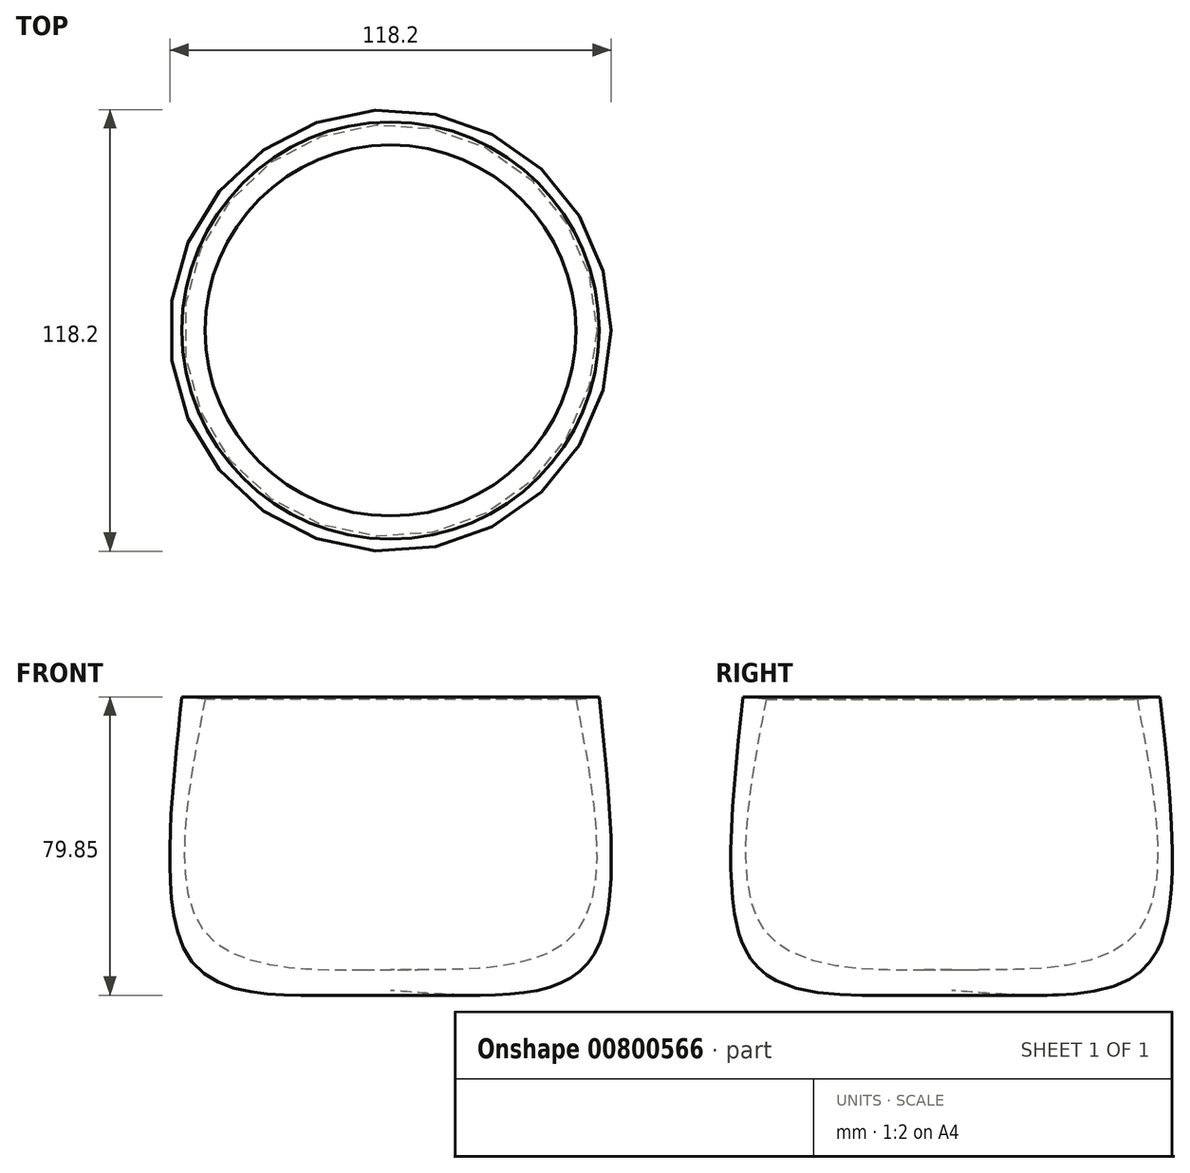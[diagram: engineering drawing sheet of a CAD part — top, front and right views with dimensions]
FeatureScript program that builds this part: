
annotation { "Feature Type Name" : "Feature", "Feature Type Description" : "" }
export const myFeature = defineFeature(function(context is Context, id is Id, definition is map)
    precondition{}
    {
        {
            var Q0;
            Q0=qCreatedBy(makeId("Front.planeOp"),FACE);
            var sketch = newSketch(context, id + "F0", { "sketchPlane" : qUnion([Q0])});
            skLineSegment(sketch, "E0", {"start": v(0, 34.35) * mm, "end": v(0, -41.15) * mm});
            skFitSpline(sketch, "E1", {"points": [v(55.85, 42.4) * mm, v(55.85, -23.83) * mm, v(39.14, -36.2) * mm, v(0, -36.2) * mm], "startDerivative": vector(19.68, -184.86) * mm, "endDerivative": vector(-129.6, 9.92) * mm});
            skFitSpline(sketch, "E2", {"points": [v(49.66, 41.77) * mm, v(49.04, -21.35) * mm, v(14.39, -30.63) * mm, v(0, -30.63) * mm], "startDerivative": vector(32.8, -172.88) * mm, "endDerivative": vector(-55.4, 0.65) * mm});
            skFitSpline(sketch, "E3", {"points": [v(49.66, 41.77) * mm, v(55.85, 42.4) * mm], "startDerivative": vector(6.19, 0.62) * mm, "endDerivative": vector(6.19, 0.62) * mm});
            skSolve(sketch);
        }
        {
            var Q0;
            {var subQ0=sQuery(id+"F0.wireOp",EDGE,"E1");Q0=makeQuery(id+"F0.imprint","IMPRINT",FACE,{"disambiguationData":[TD([[makeQuery(id+"F0.imprint","IMPRINT",EDGE,{"derivedFrom":subQ0}),-1.0]])]});}
            var Q1;
            Q1=sQuery(id+"F0.wireOp",EDGE,"E0");
            revolve(context, id + "F1", {"surfaceOperationType" : NewSurfaceOperationType.NEW, "entities" : qUnion([Q0]), "axis" : qUnion([Q1]), "revolveType" : RevolveType.FULL});
        }
        {
            var Q0;
            Q0=qCreatedBy(makeId("Front.planeOp"),FACE);
            var sketch = newSketch(context, id + "F2", { "sketchPlane" : qUnion([Q0])});
            skLineSegment(sketch, "E4", {"start": v(35.43, 29.4) * mm, "end": v(60.7, 29.4) * mm});
            skLineSegment(sketch, "E5", {"start": v(75.7, 14.4) * mm, "end": v(75.7, -14.4) * mm});
            skLineSegment(sketch, "E6", {"start": v(60.7, -29.4) * mm, "end": v(36.05, -29.4) * mm});
            skPoint(sketch, "E7.visualSharp", {"position": v(75.7, 29.4) * mm});
            skArc(sketch, "E7.filletArc", {"start": v(75.7, 14.4) * mm, "mid": v(71.31, 25) * mm, "end": v(60.7, 29.4) * mm});
            skPoint(sketch, "E8.visualSharp", {"position": v(75.7, -29.4) * mm});
            skArc(sketch, "E8.filletArc", {"start": v(60.7, -29.4) * mm, "mid": v(71.31, -25) * mm, "end": v(75.7, -14.4) * mm});
            skLineSegment(sketch, "E9", {"start": v(0, 29.4) * mm, "end": v(0, -30.46) * mm});
            skLineSegment(sketch, "E10", {"start": v(35.43, 29.4) * mm, "end": v(14.03, 29.4) * mm});
            skLineSegment(sketch, "E11", {"start": v(14.03, 29.4) * mm, "end": v(14.03, -30) * mm});
            skLineSegment(sketch, "E12", {"start": v(14.03, -30) * mm, "end": v(36.05, -29.4) * mm});
            skSolve(sketch);
        }
        {
            var Q0;
            Q0=qCreatedBy(makeId("Right.planeOp"),FACE);
            var sketch = newSketch(context, id + "F3", { "sketchPlane" : qUnion([Q0])});
            skCircle(sketch, "E13", {"center": v(197.25, 38.45) * mm, "radius": 3.87 * mm});
            skCircle(sketch, "E14", {"center": v(0, -30.43) * mm, "radius": 6.75 * mm});
            skCircle(sketch, "E15", {"center": v(0, 28.97) * mm, "radius": 5.76 * mm});
            skSolve(sketch);
        }
        {
            var Q0;
            Q0=makeQuery(id+"F3.imprint","IMPRINT",FACE,{"disambiguationData":[TD([[makeQuery(id+"F3.imprint","IMPRINT",EDGE,{"derivedFrom":sQuery(id+"F3.wireOp",EDGE,"E15")}),1.0]])]});
            var Q1;
            Q1=sQuery(id+"F3.wireOp",EDGE,"E15");
            var Q2;
            Q2=sQuery(id+"F2.wireOp",EDGE,"E10");
            var Q3;
            Q3=sQuery(id+"F2.wireOp",EDGE,"E4");
            var Q4;
            Q4=sQuery(id+"F2.wireOp",EDGE,"E7.filletArc");
            var Q5;
            Q5=sQuery(id+"F2.wireOp",EDGE,"E5");
            var Q6;
            Q6=sQuery(id+"F2.wireOp",EDGE,"E8.filletArc");
            var Q7;
            Q7=sQuery(id+"F2.wireOp",EDGE,"E6");
            var Q8;
            Q8=sQuery(id+"F2.wireOp",EDGE,"E12");
            sweep(context, id + "F4", {"profiles" : qUnion([Q0]), "surfaceProfiles" : qUnion([Q1]), "path" : qUnion([Q2, Q3, Q4, Q5, Q6, Q7, Q8])});
        }
        {
            var Q0;
            Q0=qCreatedBy(makeId("Front.planeOp"),FACE);
            var sketch = newSketch(context, id + "F5", { "sketchPlane" : qUnion([Q0])});
            skText(sketch, "E16", { "text": "KHL", "fontName": "OpenSans-Regular.ttf"});
            const initialGuessF5  = {"E16": [-0.04052, -0.01345, 1, 0, 0.03693]};
            skSetInitialGuess(sketch, initialGuessF5);
            skSolve(sketch);
        }
        {
            var Q0;
            Q0 = qSketchRegion(id + "F5", true);
            extrude(context, id + "F6", {"entities" : qUnion([Q0]), "depth" : 60 * mm, "offsetDistance" : 25 * mm});
        }
        {
            var Q0;
            Q0=makeQuery(id+"F1.opRevolve","SWEPT_BODY",BODY,{"disambiguationData":[OSD([sQuery(id+"F0.wireOp",EDGE,"E0"),sQuery(id+"F0.wireOp",EDGE,"E1"),sQuery(id+"F0.wireOp",EDGE,"E2"),sQuery(id+"F0.wireOp",EDGE,"E3")])]});
            var Q1;
            Q1=makeQuery(id+"F4.opSweep","SWEPT_BODY",BODY,{"disambiguationData":[OSD([sQuery(id+"F2.wireOp",EDGE,"E12"),sQuery(id+"F3.wireOp",EDGE,"E15")])]});
            booleanBodies(context, id + "F7", {"operationType" : BooleanOperationType.SUBTRACTION, "tools" : qUnion([Q0]), "targets" : qUnion([Q1]), "keepTools" : true});
        }
        {
            var Q0;
            Q0=makeQuery(id+"F7.opBoolean","SPLIT",BODY,{"disambiguationData":[OD(0.0)],"derivedFrom":makeQuery(id+"F4.opSweep","SWEPT_BODY",BODY,{"disambiguationData":[OSD([sQuery(id+"F2.wireOp",EDGE,"E12"),sQuery(id+"F3.wireOp",EDGE,"E15")])]})});
            var Q1;
            Q1=makeQuery(id+"F7.opBoolean","SPLIT",BODY,{"disambiguationData":[OD(1.0)],"derivedFrom":makeQuery(id+"F4.opSweep","SWEPT_BODY",BODY,{"disambiguationData":[OSD([sQuery(id+"F2.wireOp",EDGE,"E12"),sQuery(id+"F3.wireOp",EDGE,"E15")])]})});
            deleteBodies(context, id + "F8", {"entities" : qUnion([Q0, Q1])});
        }
        {
            var Q0;
            Q0=makeQuery(id+"F1.opRevolve","SWEPT_BODY",BODY,{"disambiguationData":[OSD([sQuery(id+"F0.wireOp",EDGE,"E0"),sQuery(id+"F0.wireOp",EDGE,"E1"),sQuery(id+"F0.wireOp",EDGE,"E2"),sQuery(id+"F0.wireOp",EDGE,"E3")])]});
            var Q1;
            Q1=makeQuery(id+"F6.opExtrude","SWEPT_BODY",BODY,{"disambiguationData":[OSD([sQuery(id+"F5.wireOp",EDGE,"E16.sketch_text.stroke-0"),sQuery(id+"F5.wireOp",EDGE,"E16.sketch_text.stroke-1"),sQuery(id+"F5.wireOp",EDGE,"E16.sketch_text.stroke-2"),sQuery(id+"F5.wireOp",EDGE,"E16.sketch_text.stroke-3"),sQuery(id+"F5.wireOp",EDGE,"E16.sketch_text.stroke-4"),sQuery(id+"F5.wireOp",EDGE,"E16.sketch_text.stroke-5"),sQuery(id+"F5.wireOp",EDGE,"E16.sketch_text.stroke-6"),sQuery(id+"F5.wireOp",EDGE,"E16.sketch_text.stroke-7"),sQuery(id+"F5.wireOp",EDGE,"E16.sketch_text.stroke-8"),sQuery(id+"F5.wireOp",EDGE,"E16.sketch_text.stroke-9"),sQuery(id+"F5.wireOp",EDGE,"E16.sketch_text.stroke-10"),sQuery(id+"F5.wireOp",EDGE,"E16.sketch_text.stroke-11")])]});
            var Q2;
            Q2=makeQuery(id+"F6.opExtrude","SWEPT_BODY",BODY,{"disambiguationData":[OSD([sQuery(id+"F5.wireOp",EDGE,"E16.sketch_text.stroke-12"),sQuery(id+"F5.wireOp",EDGE,"E16.sketch_text.stroke-13"),sQuery(id+"F5.wireOp",EDGE,"E16.sketch_text.stroke-14"),sQuery(id+"F5.wireOp",EDGE,"E16.sketch_text.stroke-15"),sQuery(id+"F5.wireOp",EDGE,"E16.sketch_text.stroke-16"),sQuery(id+"F5.wireOp",EDGE,"E16.sketch_text.stroke-17"),sQuery(id+"F5.wireOp",EDGE,"E16.sketch_text.stroke-18"),sQuery(id+"F5.wireOp",EDGE,"E16.sketch_text.stroke-19"),sQuery(id+"F5.wireOp",EDGE,"E16.sketch_text.stroke-20"),sQuery(id+"F5.wireOp",EDGE,"E16.sketch_text.stroke-21"),sQuery(id+"F5.wireOp",EDGE,"E16.sketch_text.stroke-22"),sQuery(id+"F5.wireOp",EDGE,"E16.sketch_text.stroke-23")])]});
            var Q3;
            Q3=makeQuery(id+"F6.opExtrude","SWEPT_BODY",BODY,{"disambiguationData":[OSD([sQuery(id+"F5.wireOp",EDGE,"E16.sketch_text.stroke-24"),sQuery(id+"F5.wireOp",EDGE,"E16.sketch_text.stroke-25"),sQuery(id+"F5.wireOp",EDGE,"E16.sketch_text.stroke-26"),sQuery(id+"F5.wireOp",EDGE,"E16.sketch_text.stroke-27"),sQuery(id+"F5.wireOp",EDGE,"E16.sketch_text.stroke-28"),sQuery(id+"F5.wireOp",EDGE,"E16.sketch_text.stroke-29")])]});
            booleanBodies(context, id + "F9", {"operationType" : BooleanOperationType.SUBTRACTION, "tools" : qUnion([Q0]), "targets" : qUnion([Q1, Q2, Q3]), "keepTools" : true});
        }
        {
            var Q0;
            Q0=makeQuery(id+"F9.opBoolean","SPLIT",BODY,{"disambiguationData":[OD(0.0)],"derivedFrom":makeQuery(id+"F6.opExtrude","SWEPT_BODY",BODY,{"disambiguationData":[OSD([sQuery(id+"F5.wireOp",EDGE,"E16.sketch_text.stroke-0"),sQuery(id+"F5.wireOp",EDGE,"E16.sketch_text.stroke-1"),sQuery(id+"F5.wireOp",EDGE,"E16.sketch_text.stroke-2"),sQuery(id+"F5.wireOp",EDGE,"E16.sketch_text.stroke-3"),sQuery(id+"F5.wireOp",EDGE,"E16.sketch_text.stroke-4"),sQuery(id+"F5.wireOp",EDGE,"E16.sketch_text.stroke-5"),sQuery(id+"F5.wireOp",EDGE,"E16.sketch_text.stroke-6"),sQuery(id+"F5.wireOp",EDGE,"E16.sketch_text.stroke-7"),sQuery(id+"F5.wireOp",EDGE,"E16.sketch_text.stroke-8"),sQuery(id+"F5.wireOp",EDGE,"E16.sketch_text.stroke-9"),sQuery(id+"F5.wireOp",EDGE,"E16.sketch_text.stroke-10"),sQuery(id+"F5.wireOp",EDGE,"E16.sketch_text.stroke-11")])]})});
            var Q1;
            Q1=makeQuery(id+"F9.opBoolean","SPLIT",BODY,{"disambiguationData":[OD(0.0)],"derivedFrom":makeQuery(id+"F6.opExtrude","SWEPT_BODY",BODY,{"disambiguationData":[OSD([sQuery(id+"F5.wireOp",EDGE,"E16.sketch_text.stroke-12"),sQuery(id+"F5.wireOp",EDGE,"E16.sketch_text.stroke-13"),sQuery(id+"F5.wireOp",EDGE,"E16.sketch_text.stroke-14"),sQuery(id+"F5.wireOp",EDGE,"E16.sketch_text.stroke-15"),sQuery(id+"F5.wireOp",EDGE,"E16.sketch_text.stroke-16"),sQuery(id+"F5.wireOp",EDGE,"E16.sketch_text.stroke-17"),sQuery(id+"F5.wireOp",EDGE,"E16.sketch_text.stroke-18"),sQuery(id+"F5.wireOp",EDGE,"E16.sketch_text.stroke-19"),sQuery(id+"F5.wireOp",EDGE,"E16.sketch_text.stroke-20"),sQuery(id+"F5.wireOp",EDGE,"E16.sketch_text.stroke-21"),sQuery(id+"F5.wireOp",EDGE,"E16.sketch_text.stroke-22"),sQuery(id+"F5.wireOp",EDGE,"E16.sketch_text.stroke-23")])]})});
            var Q2;
            Q2=makeQuery(id+"F9.opBoolean","SPLIT",BODY,{"disambiguationData":[OD(1.0)],"derivedFrom":makeQuery(id+"F6.opExtrude","SWEPT_BODY",BODY,{"disambiguationData":[OSD([sQuery(id+"F5.wireOp",EDGE,"E16.sketch_text.stroke-24"),sQuery(id+"F5.wireOp",EDGE,"E16.sketch_text.stroke-25"),sQuery(id+"F5.wireOp",EDGE,"E16.sketch_text.stroke-26"),sQuery(id+"F5.wireOp",EDGE,"E16.sketch_text.stroke-27"),sQuery(id+"F5.wireOp",EDGE,"E16.sketch_text.stroke-28"),sQuery(id+"F5.wireOp",EDGE,"E16.sketch_text.stroke-29")])]})});
            deleteBodies(context, id + "F10", {"entities" : qUnion([Q0, Q1, Q2])});
        }
    });
